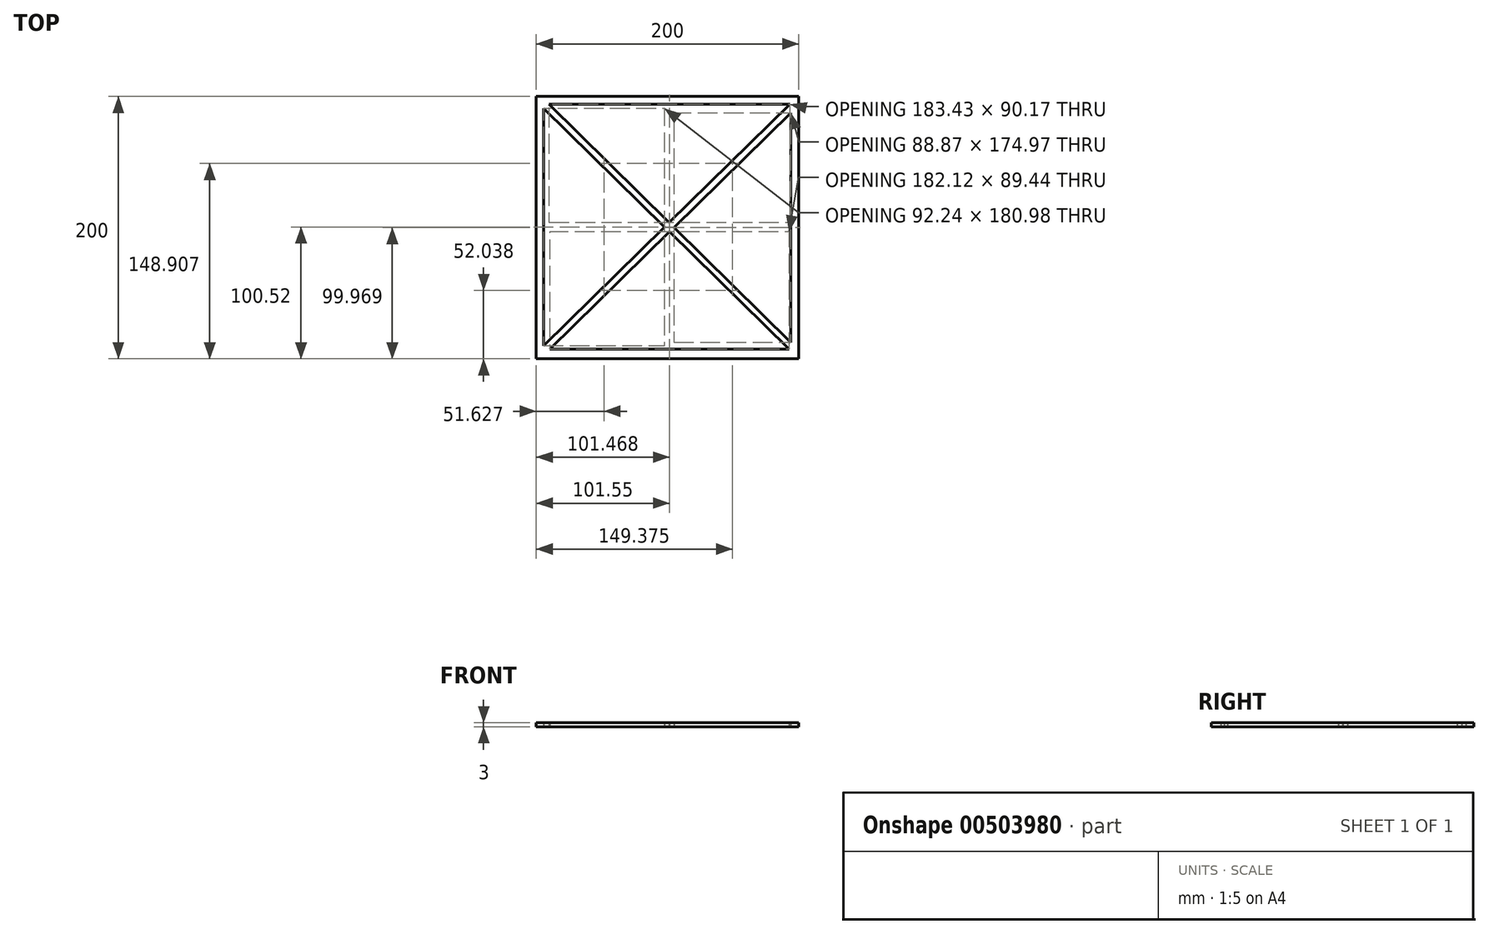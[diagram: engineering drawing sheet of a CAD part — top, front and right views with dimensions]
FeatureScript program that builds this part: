
annotation { "Feature Type Name" : "Feature", "Feature Type Description" : "" }
export const myFeature = defineFeature(function(context is Context, id is Id, definition is map)
    precondition{}
    {
        {
            var Q0;
            Q0=qCreatedBy(makeId("Top.planeOp"),FACE);
            var sketch = newSketch(context, id + "F0", { "sketchPlane" : qUnion([Q0])});
            skLineSegment(sketch, "E0.bottom", {"start": v(-100.15, 112.6) * mm, "end": v(99.85, 112.6) * mm});
            skLineSegment(sketch, "E0.top", {"start": v(-100.15, -87.4) * mm, "end": v(99.85, -87.4) * mm});
            skLineSegment(sketch, "E0.left", {"start": v(-100.15, 112.6) * mm, "end": v(-100.15, -87.4) * mm});
            skLineSegment(sketch, "E0.right", {"start": v(99.85, 112.6) * mm, "end": v(99.85, -87.4) * mm});
            skLineSegment(sketch, "E1.bottom", {"start": v(-90.31, 106.6) * mm, "end": v(93.11, 106.6) * mm});
            skLineSegment(sketch, "E1.top", {"start": v(-89.74, -80.08) * mm, "end": v(92.38, -80.08) * mm});
            skLineSegment(sketch, "E1.left", {"start": v(-94.64, 103.61) * mm, "end": v(-94.64, -77.37) * mm});
            skLineSegment(sketch, "E1.right", {"start": v(93.66, 100.06) * mm, "end": v(93.66, -74.92) * mm});
            skLineSegment(sketch, "E2", {"start": v(-90.31, 106.6) * mm, "end": v(1.08, 16.42) * mm});
            skLineSegment(sketch, "E3", {"start": v(-94.64, 103.61) * mm, "end": v(-2.4, 13) * mm});
            skLineSegment(sketch, "E4", {"start": v(93.11, 106.6) * mm, "end": v(1.08, 16.42) * mm});
            skLineSegment(sketch, "E5", {"start": v(93.66, 100.06) * mm, "end": v(4.79, 12.77) * mm});
            skLineSegment(sketch, "E6.trimOffspring", {"start": v(-2.4, 13) * mm, "end": v(-94.64, -77.37) * mm});
            skLineSegment(sketch, "E7.trimOffspring", {"start": v(4.79, 12.77) * mm, "end": v(93.66, -74.92) * mm});
            skLineSegment(sketch, "E8.trimOffspring", {"start": v(1.32, 9.36) * mm, "end": v(-89.74, -80.08) * mm});
            skLineSegment(sketch, "E9.trimOffspring", {"start": v(1.32, 9.36) * mm, "end": v(92.38, -80.08) * mm});
            skSolve(sketch);
        }
        {
            var Q0;
            Q0=qSketchRegion(id+"F0",true);
            extrude(context, id + "F1", {"entities" : qUnion([Q0]), "depth" : 3 * mm});
        }
    });
